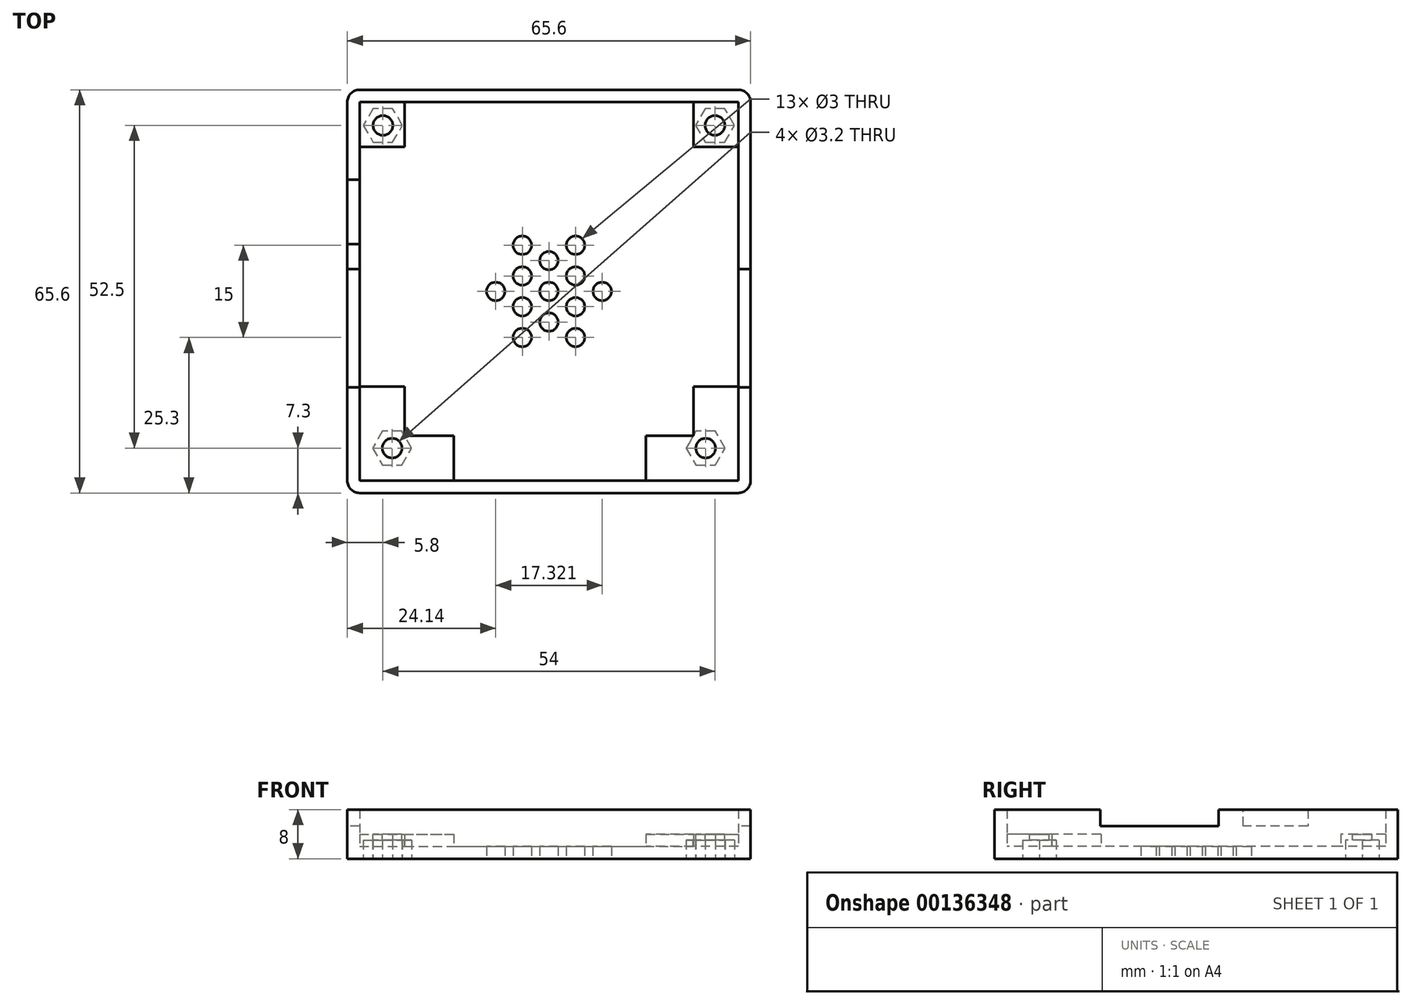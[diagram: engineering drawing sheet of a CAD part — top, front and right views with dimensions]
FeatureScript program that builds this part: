
annotation { "Feature Type Name" : "Feature", "Feature Type Description" : "" }
export const myFeature = defineFeature(function(context is Context, id is Id, definition is map)
    precondition{}
    {
        {
            var Q0;
            Q0=qCreatedBy(makeId("Top.planeOp"),FACE);
            var sketch = newSketch(context, id + "F0", { "sketchPlane" : qUnion([Q0])});
            skLineSegment(sketch, "E0.bottom", {"start": v(0, 0) * mm, "end": v(61, 0) * mm, "construction": true});
            skLineSegment(sketch, "E0.top", {"start": v(0, -61) * mm, "end": v(61, -61) * mm, "construction": true});
            skLineSegment(sketch, "E0.left", {"start": v(0, 0) * mm, "end": v(0, -61) * mm, "construction": true});
            skLineSegment(sketch, "E0.right", {"start": v(61, 0) * mm, "end": v(61, -61) * mm, "construction": true});
            skLineSegment(sketch, "E1.0", {"start": v(-0.3, 0.3) * mm, "end": v(61.3, 0.3) * mm});
            skLineSegment(sketch, "E1.1", {"start": v(-0.3, 0.3) * mm, "end": v(-0.3, -61.3) * mm});
            skLineSegment(sketch, "E1.2", {"start": v(-0.3, -61.3) * mm, "end": v(61.3, -61.3) * mm});
            skLineSegment(sketch, "E1.3", {"start": v(61.3, 0.3) * mm, "end": v(61.3, -61.3) * mm});
            skCircle(sketch, "E2", {"center": v(3.5, -3.5) * mm, "radius": 1.6 * mm});
            skCircle(sketch, "E3", {"center": v(57.5, -3.5) * mm, "radius": 1.6 * mm});
            skLineSegment(sketch, "E4", {"start": v(3.5, -3.5) * mm, "end": v(57.5, -3.5) * mm, "construction": true});
            skLineSegment(sketch, "E5.0", {"start": v(-2.3, 2.3) * mm, "end": v(63.3, 2.3) * mm});
            skLineSegment(sketch, "E5.1", {"start": v(-2.3, 2.3) * mm, "end": v(-2.3, -63.3) * mm});
            skLineSegment(sketch, "E5.2", {"start": v(-2.3, -63.3) * mm, "end": v(63.3, -63.3) * mm});
            skLineSegment(sketch, "E5.3", {"start": v(63.3, 2.3) * mm, "end": v(63.3, -63.3) * mm});
            skCircle(sketch, "E6", {"center": v(5, -56) * mm, "radius": 1.6 * mm});
            skCircle(sketch, "E7", {"center": v(56, -56) * mm, "radius": 1.6 * mm});
            skLineSegment(sketch, "E8", {"start": v(5, -56) * mm, "end": v(56, -56) * mm, "construction": true});
            skSolve(sketch);
        }
        {
            var Q0;
            Q0=makeQuery(id+"F0.imprint","IMPRINT",FACE,{"disambiguationData":[TD([[makeQuery(id+"F0.imprint","IMPRINT",EDGE,{"derivedFrom":sQuery(id+"F0.wireOp",EDGE,"E1.0")}),1.0]])]});
            var Q1;
            Q1=makeQuery(id+"F0.imprint","IMPRINT",FACE,{"disambiguationData":[TD([[makeQuery(id+"F0.imprint","IMPRINT",EDGE,{"derivedFrom":sQuery(id+"F0.wireOp",EDGE,"E1.0")}),-1.0]])]});
            extrude(context, id + "F1", {"entities" : qUnion([Q0, Q1]), "oppositeDirection" : true, "depth" : 2 * mm});
        }
        {
            var Q0;
            Q0 = qSketchRegion(id + "F0", true);
            extrude(context, id + "F2", {"entities" : qUnion([Q0]), "operationType" : NewBodyOperationType.ADD, "depth" : 6 * mm});
        }
        {
            var Q0;
            Q0=makeQuery(id+"F1.opExtrude","CAP_FACE",FACE,{"disambiguationData":[OSD([sQuery(id+"F0.wireOp",EDGE,"E1.0"),sQuery(id+"F0.wireOp",EDGE,"E1.1"),sQuery(id+"F0.wireOp",EDGE,"E1.2"),sQuery(id+"F0.wireOp",EDGE,"E1.3"),sQuery(id+"F0.wireOp",EDGE,"E2"),sQuery(id+"F0.wireOp",EDGE,"E3")])],"isStart":true});
            var sketch = newSketch(context, id + "F3", { "sketchPlane" : qUnion([Q0])});
            skLineSegment(sketch, "E9.bottom", {"start": v(61.3, 0.3) * mm, "end": v(54, 0.3) * mm});
            skLineSegment(sketch, "E9.top", {"start": v(61.3, -7) * mm, "end": v(54, -7) * mm});
            skLineSegment(sketch, "E9.left", {"start": v(61.3, 0.3) * mm, "end": v(61.3, -7) * mm});
            skLineSegment(sketch, "E9.right", {"start": v(54, 0.3) * mm, "end": v(54, -7) * mm});
            skLineSegment(sketch, "E10.bottom", {"start": v(-0.3, 0.3) * mm, "end": v(7, 0.3) * mm});
            skLineSegment(sketch, "E10.top", {"start": v(-0.3, -7) * mm, "end": v(7, -7) * mm});
            skLineSegment(sketch, "E10.left", {"start": v(-0.3, 0.3) * mm, "end": v(-0.3, -7) * mm});
            skLineSegment(sketch, "E10.right", {"start": v(7, 0.3) * mm, "end": v(7, -7) * mm});
            skLineSegment(sketch, "E11", {"start": v(-0.3, -46) * mm, "end": v(7, -46) * mm});
            skLineSegment(sketch, "E12", {"start": v(7, -46) * mm, "end": v(7, -54) * mm});
            skLineSegment(sketch, "E13", {"start": v(7, -54) * mm, "end": v(15, -54) * mm});
            skLineSegment(sketch, "E14", {"start": v(15, -54) * mm, "end": v(15, -61.3) * mm});
            skLineSegment(sketch, "E15", {"start": v(15, -61.3) * mm, "end": v(-0.3, -61.3) * mm});
            skLineSegment(sketch, "E16", {"start": v(-0.3, -61.3) * mm, "end": v(-0.3, -46) * mm});
            skLineSegment(sketch, "E17", {"start": v(7, -7) * mm, "end": v(7, -46) * mm, "construction": true});
            skLineSegment(sketch, "E18", {"start": v(61.3, -46) * mm, "end": v(54, -46) * mm});
            skLineSegment(sketch, "E19", {"start": v(54, -46) * mm, "end": v(54, -54) * mm});
            skLineSegment(sketch, "E20", {"start": v(54, -54) * mm, "end": v(46.3, -54) * mm});
            skLineSegment(sketch, "E21", {"start": v(46.3, -54) * mm, "end": v(46.3, -61.3) * mm});
            skLineSegment(sketch, "E22", {"start": v(15, -54) * mm, "end": v(46.3, -54) * mm, "construction": true});
            skLineSegment(sketch, "E23", {"start": v(54, -7) * mm, "end": v(54, -46) * mm, "construction": true});
            skLineSegment(sketch, "E24", {"start": v(46.3, -61.3) * mm, "end": v(61.3, -61.3) * mm});
            skLineSegment(sketch, "E25", {"start": v(61.3, -61.3) * mm, "end": v(61.3, -46) * mm});
            skLineSegment(sketch, "E26", {"start": v(7, -46) * mm, "end": v(54, -46) * mm, "construction": true});
            skSolve(sketch);
        }
        {
            var Q0;
            Q0 = qSketchRegion(id + "F3", true);
            extrude(context, id + "F4", {"entities" : qUnion([Q0]), "operationType" : NewBodyOperationType.ADD, "depth" : 2 * mm});
        }
        {
            var Q0;
            Q0=makeQuery(id+"F0.imprint","IMPRINT",FACE,{"disambiguationData":[TD([[makeQuery(id+"F0.imprint","IMPRINT",EDGE,{"derivedFrom":sQuery(id+"F0.wireOp",EDGE,"E2")}),1.0]])]});
            var Q1;
            Q1=makeQuery(id+"F0.imprint","IMPRINT",FACE,{"disambiguationData":[TD([[makeQuery(id+"F0.imprint","IMPRINT",EDGE,{"derivedFrom":sQuery(id+"F0.wireOp",EDGE,"E3")}),1.0]])]});
            var Q2;
            Q2=makeQuery(id+"F0.imprint","IMPRINT",FACE,{"disambiguationData":[TD([[makeQuery(id+"F0.imprint","IMPRINT",EDGE,{"derivedFrom":sQuery(id+"F0.wireOp",EDGE,"E6")}),1.0]])]});
            var Q3;
            Q3=makeQuery(id+"F0.imprint","IMPRINT",FACE,{"disambiguationData":[TD([[makeQuery(id+"F0.imprint","IMPRINT",EDGE,{"derivedFrom":sQuery(id+"F0.wireOp",EDGE,"E7")}),1.0]])]});
            var Q4;
            Q4 = qConstructionFilter(qBodyType(qCreatedBy(id + "F0" ,EDGE), BodyType.WIRE), ConstructionObject.NO);
            extrude(context, id + "F5", {"entities" : qUnion([Q0, Q1, Q2, Q3]), "operationType" : NewBodyOperationType.REMOVE, "surfaceEntities" : qUnion([Q4]), "endBound" : BoundingType.THROUGH_ALL, "depth" : 25 * mm});
        }
        {
            var Q0;
            Q0=makeQuery(id+"F2.opExtrude","SWEPT_FACE",FACE,{"disambiguationData":[OSD([sQuery(id+"F0.wireOp",EDGE,"E1.3")])]});
            var sketch = newSketch(context, id + "F6", { "sketchPlane" : qUnion([Q0])});
            skLineSegment(sketch, "E27", {"start": v(46, 2) * mm, "end": v(7, 2) * mm, "construction": true});
            skLineSegment(sketch, "E28.bottom", {"start": v(46.12, 3.3) * mm, "end": v(26.87, 3.3) * mm});
            skLineSegment(sketch, "E28.top", {"start": v(46.12, 6) * mm, "end": v(26.87, 6) * mm});
            skLineSegment(sketch, "E28.left", {"start": v(46.12, 3.3) * mm, "end": v(46.12, 6) * mm});
            skLineSegment(sketch, "E28.right", {"start": v(26.87, 3.3) * mm, "end": v(26.87, 6) * mm});
            skSolve(sketch);
        }
        {
            var Q0;
            Q0 = qSketchRegion(id + "F6", true);
            extrude(context, id + "F7", {"entities" : qUnion([Q0]), "operationType" : NewBodyOperationType.REMOVE, "endBound" : BoundingType.THROUGH_ALL, "oppositeDirection" : true, "depth" : 25 * mm, "hasSecondDirection" : true, "secondDirectionBound" : SecondDirectionBoundingType.THROUGH_ALL, "secondDirectionOppositeDirection" : false, "secondDirectionDepth" : 25 * mm});
        }
        {
            var Q0;
            Q0=makeQuery(id+"F2.opExtrude","SWEPT_FACE",FACE,{"disambiguationData":[OSD([sQuery(id+"F0.wireOp",EDGE,"E1.1")])]});
            var sketch = newSketch(context, id + "F8", { "sketchPlane" : qUnion([Q0])});
            skLineSegment(sketch, "E29", {"start": v(-22.84, 6) * mm, "end": v(-22.84, 3.3) * mm});
            skLineSegment(sketch, "E30", {"start": v(-22.84, 3.3) * mm, "end": v(-12.34, 3.31) * mm});
            skLineSegment(sketch, "E31", {"start": v(-12.34, 3.31) * mm, "end": v(-12.34, 6) * mm});
            skLineSegment(sketch, "E32", {"start": v(-22.84, 6) * mm, "end": v(-12.34, 6) * mm});
            skSolve(sketch);
        }
        {
            var Q0;
            Q0 = qSketchRegion(id + "F8", true);
            extrude(context, id + "F9", {"entities" : qUnion([Q0]), "operationType" : NewBodyOperationType.REMOVE, "endBound" : BoundingType.THROUGH_ALL, "oppositeDirection" : true, "depth" : 25 * mm});
        }
        {
            var Q0;
            Q0=makeQuery(id+"F1.opExtrude","CAP_FACE",FACE,{"disambiguationData":[OSD([sQuery(id+"F0.wireOp",EDGE,"E2"),sQuery(id+"F0.wireOp",EDGE,"E3"),sQuery(id+"F0.wireOp",EDGE,"E5.0"),sQuery(id+"F0.wireOp",EDGE,"E5.1"),sQuery(id+"F0.wireOp",EDGE,"E5.2"),sQuery(id+"F0.wireOp",EDGE,"E5.3")])],"isStart":false});
            var sketch = newSketch(context, id + "F10", { "sketchPlane" : qUnion([Q0])});
            skCircle(sketch, "E33.cCircle", {"center": v(3.5, 3.5) * mm, "radius": 2.75 * mm, "construction": true});
            skLineSegment(sketch, "E33.0", {"start": v(0.32, 3.5) * mm, "end": v(1.91, 6.25) * mm});
            skLineSegment(sketch, "E33.1", {"start": v(1.91, 6.25) * mm, "end": v(5.09, 6.25) * mm});
            skLineSegment(sketch, "E33.2", {"start": v(5.09, 6.25) * mm, "end": v(6.68, 3.5) * mm});
            skLineSegment(sketch, "E33.3", {"start": v(6.68, 3.5) * mm, "end": v(5.09, 0.75) * mm});
            skLineSegment(sketch, "E33.4", {"start": v(5.09, 0.75) * mm, "end": v(1.91, 0.75) * mm});
            skLineSegment(sketch, "E33.5", {"start": v(1.91, 0.75) * mm, "end": v(0.32, 3.5) * mm});
            skPoint(sketch, "E33.0.midPoint", {"position": v(1.12, 4.88) * mm});
            skCircle(sketch, "E34.cCircle", {"center": v(57.5, 3.5) * mm, "radius": 2.75 * mm, "construction": true});
            skLineSegment(sketch, "E34.0", {"start": v(59.09, 0.75) * mm, "end": v(55.91, 0.75) * mm});
            skLineSegment(sketch, "E34.1", {"start": v(55.91, 0.75) * mm, "end": v(54.32, 3.5) * mm});
            skLineSegment(sketch, "E34.2", {"start": v(54.32, 3.5) * mm, "end": v(55.91, 6.25) * mm});
            skLineSegment(sketch, "E34.3", {"start": v(55.91, 6.25) * mm, "end": v(59.09, 6.25) * mm});
            skLineSegment(sketch, "E34.4", {"start": v(59.09, 6.25) * mm, "end": v(60.68, 3.5) * mm});
            skLineSegment(sketch, "E34.5", {"start": v(60.68, 3.5) * mm, "end": v(59.09, 0.75) * mm});
            skPoint(sketch, "E34.0.midPoint", {"position": v(57.5, 0.75) * mm});
            skCircle(sketch, "E35.cCircle", {"center": v(5, 56) * mm, "radius": 2.75 * mm, "construction": true});
            skLineSegment(sketch, "E35.0", {"start": v(8.18, 56) * mm, "end": v(6.59, 53.25) * mm});
            skLineSegment(sketch, "E35.1", {"start": v(6.59, 53.25) * mm, "end": v(3.41, 53.25) * mm});
            skLineSegment(sketch, "E35.2", {"start": v(3.41, 53.25) * mm, "end": v(1.82, 56) * mm});
            skLineSegment(sketch, "E35.3", {"start": v(1.82, 56) * mm, "end": v(3.41, 58.75) * mm});
            skLineSegment(sketch, "E35.4", {"start": v(3.41, 58.75) * mm, "end": v(6.59, 58.75) * mm});
            skLineSegment(sketch, "E35.5", {"start": v(6.59, 58.75) * mm, "end": v(8.18, 56) * mm});
            skPoint(sketch, "E35.0.midPoint", {"position": v(7.38, 54.63) * mm});
            skCircle(sketch, "E36.cCircle", {"center": v(56, 56) * mm, "radius": 2.75 * mm, "construction": true});
            skLineSegment(sketch, "E36.0", {"start": v(57.59, 53.25) * mm, "end": v(54.41, 53.25) * mm});
            skLineSegment(sketch, "E36.1", {"start": v(54.41, 53.25) * mm, "end": v(52.82, 56) * mm});
            skLineSegment(sketch, "E36.2", {"start": v(52.82, 56) * mm, "end": v(54.41, 58.75) * mm});
            skLineSegment(sketch, "E36.3", {"start": v(54.41, 58.75) * mm, "end": v(57.59, 58.75) * mm});
            skLineSegment(sketch, "E36.4", {"start": v(57.59, 58.75) * mm, "end": v(59.18, 56) * mm});
            skLineSegment(sketch, "E36.5", {"start": v(59.18, 56) * mm, "end": v(57.59, 53.25) * mm});
            skPoint(sketch, "E36.0.midPoint", {"position": v(56, 53.25) * mm});
            skSolve(sketch);
        }
        {
            var Q0;
            Q0 = qSketchRegion(id + "F10", true);
            extrude(context, id + "F11", {"entities" : qUnion([Q0]), "operationType" : NewBodyOperationType.REMOVE, "oppositeDirection" : true, "depth" : 3 * mm});
        }
        {
            var Q0;
            Q0=makeQuery(id+"F1.opExtrude","CAP_FACE",FACE,{"disambiguationData":[OSD([sQuery(id+"F0.wireOp",EDGE,"E2"),sQuery(id+"F0.wireOp",EDGE,"E3"),sQuery(id+"F0.wireOp",EDGE,"E5.0"),sQuery(id+"F0.wireOp",EDGE,"E5.1"),sQuery(id+"F0.wireOp",EDGE,"E5.2"),sQuery(id+"F0.wireOp",EDGE,"E5.3"),sQuery(id+"F0.wireOp",EDGE,"E6"),sQuery(id+"F0.wireOp",EDGE,"E7")])],"isStart":false});
            var sketch = newSketch(context, id + "F12", { "sketchPlane" : qUnion([Q0])});
            skLineSegment(sketch, "E37", {"start": v(30.5, 63.3) * mm, "end": v(30.5, -2.3) * mm, "construction": true});
            skLineSegment(sketch, "E38", {"start": v(-2.3, 30.5) * mm, "end": v(63.3, 30.5) * mm, "construction": true});
            skCircle(sketch, "E39", {"center": v(30.5, 30.5) * mm, "radius": 1.5 * mm});
            skCircle(sketch, "E40", {"center": v(30.5, 35.5) * mm, "radius": 1.5 * mm});
            skCircle(sketch, "E41.1.0", {"center": v(26.17, 33) * mm, "radius": 1.5 * mm});
            skCircle(sketch, "E41.2.0", {"center": v(26.17, 28) * mm, "radius": 1.5 * mm});
            skCircle(sketch, "E41.3.0", {"center": v(30.5, 25.5) * mm, "radius": 1.5 * mm});
            skCircle(sketch, "E41.4.0", {"center": v(34.83, 28) * mm, "radius": 1.5 * mm});
            skCircle(sketch, "E41.5.0", {"center": v(34.83, 33) * mm, "radius": 1.5 * mm});
            skLineSegment(sketch, "E42", {"start": v(30.5, 30.5) * mm, "end": v(26.17, 38) * mm, "construction": true});
            skLineSegment(sketch, "E43", {"start": v(26.17, 38) * mm, "end": v(26.17, 33) * mm, "construction": true});
            skCircle(sketch, "E44", {"center": v(26.17, 38) * mm, "radius": 1.5 * mm});
            skCircle(sketch, "E45.1.0", {"center": v(21.84, 30.5) * mm, "radius": 1.5 * mm});
            skCircle(sketch, "E45.2.0", {"center": v(26.17, 23) * mm, "radius": 1.5 * mm});
            skCircle(sketch, "E45.3.0", {"center": v(34.83, 23) * mm, "radius": 1.5 * mm});
            skCircle(sketch, "E45.4.0", {"center": v(39.16, 30.5) * mm, "radius": 1.5 * mm});
            skCircle(sketch, "E45.5.0", {"center": v(34.83, 38) * mm, "radius": 1.5 * mm});
            skSolve(sketch);
        }
        {
            var Q0;
            Q0 = qSketchRegion(id + "F12", true);
            extrude(context, id + "F13", {"entities" : qUnion([Q0]), "operationType" : NewBodyOperationType.REMOVE, "endBound" : BoundingType.THROUGH_ALL, "oppositeDirection" : true, "depth" : 25 * mm});
        }
        {
            var Q0;
            {var subQ0=sQuery(id+"F0.wireOp",EDGE,"E5.2");var subQ1=sQuery(id+"F0.wireOp",EDGE,"E5.1");Q0=makeQuery(id+"F2.boolean.opBoolean","MERGE",EDGE,{"derivedFrom":[makeQuery(id+"F1.opExtrude","SWEPT_EDGE",EDGE,{"disambiguationData":[OSD([subQ1,subQ0])]}),makeQuery(id+"F2.opExtrude","SWEPT_EDGE",EDGE,{"disambiguationData":[OSD([subQ1,subQ0])]})]});}
            var Q1;
            {var subQ0=sQuery(id+"F0.wireOp",EDGE,"E5.1");var subQ1=sQuery(id+"F0.wireOp",EDGE,"E5.0");Q1=makeQuery(id+"F2.boolean.opBoolean","MERGE",EDGE,{"derivedFrom":[makeQuery(id+"F1.opExtrude","SWEPT_EDGE",EDGE,{"disambiguationData":[OSD([subQ1,subQ0])]}),makeQuery(id+"F2.opExtrude","SWEPT_EDGE",EDGE,{"disambiguationData":[OSD([subQ1,subQ0])]})]});}
            var Q2;
            {var subQ0=sQuery(id+"F0.wireOp",EDGE,"E5.3");var subQ1=sQuery(id+"F0.wireOp",EDGE,"E5.0");Q2=makeQuery(id+"F2.boolean.opBoolean","MERGE",EDGE,{"derivedFrom":[makeQuery(id+"F1.opExtrude","SWEPT_EDGE",EDGE,{"disambiguationData":[OSD([subQ1,subQ0])]}),makeQuery(id+"F2.opExtrude","SWEPT_EDGE",EDGE,{"disambiguationData":[OSD([subQ1,subQ0])]})]});}
            var Q3;
            {var subQ0=sQuery(id+"F0.wireOp",EDGE,"E5.3");var subQ1=sQuery(id+"F0.wireOp",EDGE,"E5.2");Q3=makeQuery(id+"F2.boolean.opBoolean","MERGE",EDGE,{"derivedFrom":[makeQuery(id+"F1.opExtrude","SWEPT_EDGE",EDGE,{"disambiguationData":[OSD([subQ1,subQ0])]}),makeQuery(id+"F2.opExtrude","SWEPT_EDGE",EDGE,{"disambiguationData":[OSD([subQ1,subQ0])]})]});}
            fillet(context, id + "F14", {"entities" : qUnion([Q0, Q1, Q2, Q3]), "radius" : 2 * mm, "tangentPropagation" : true, "allowEdgeOverflow" : false});
        }
    });
